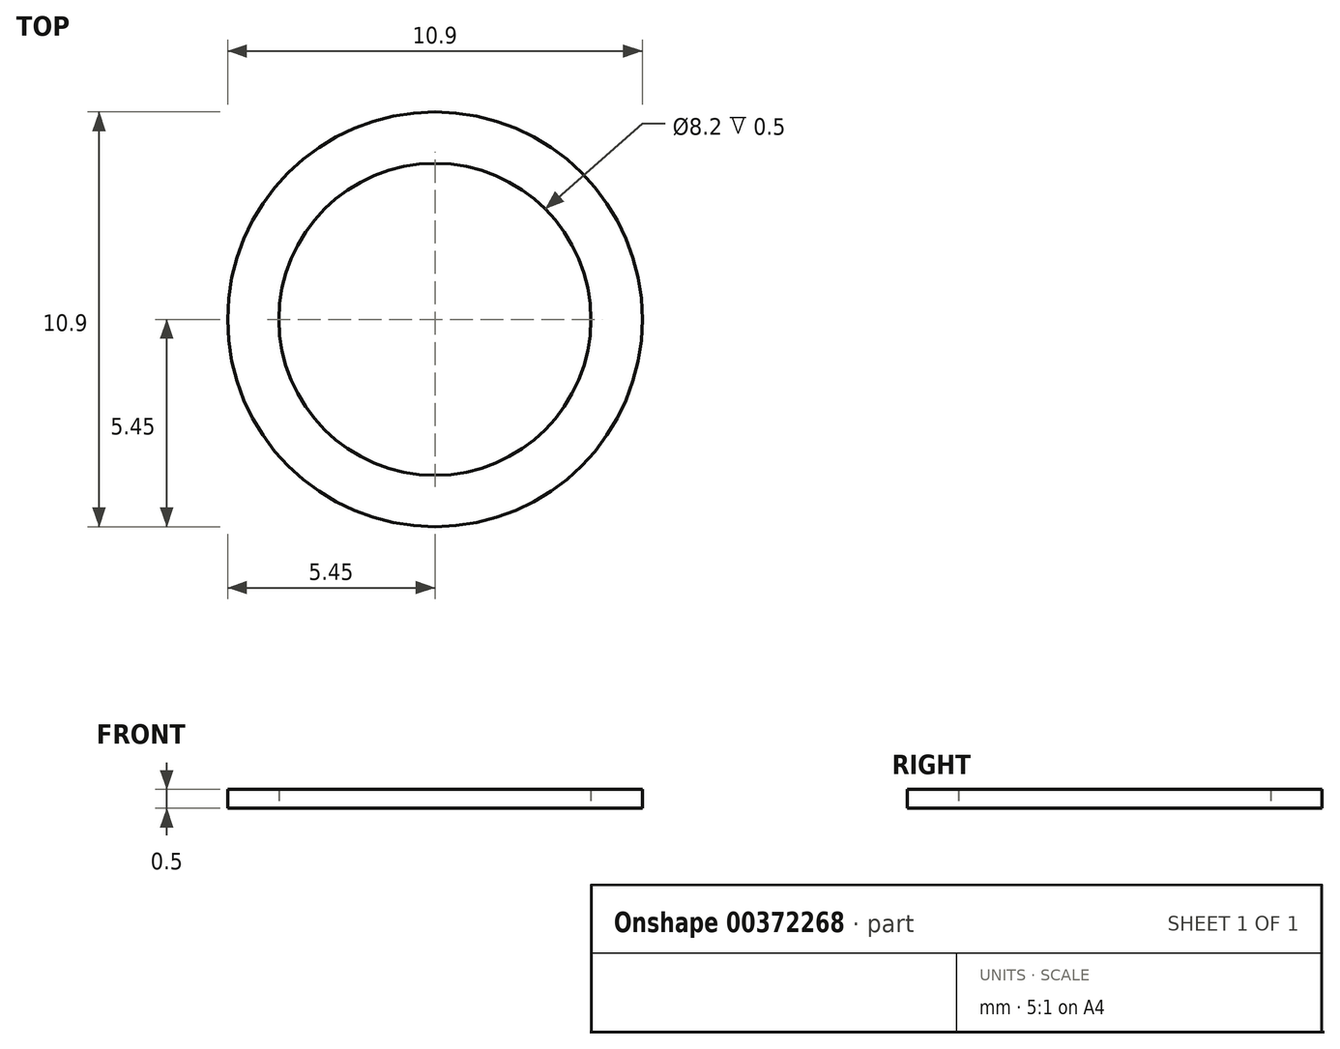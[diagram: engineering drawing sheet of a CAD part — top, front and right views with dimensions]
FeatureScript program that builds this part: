
annotation { "Feature Type Name" : "Feature", "Feature Type Description" : "" }
export const myFeature = defineFeature(function(context is Context, id is Id, definition is map)
    precondition{}
    {
        {
            var Q0;
            Q0=qCreatedBy(makeId("Top.planeOp"),FACE);
            var sketch = newSketch(context, id + "F0", { "sketchPlane" : qUnion([Q0])});
            skCircle(sketch, "E0", {"center": v(0, 0) * mm, "radius": 4.1 * mm});
            skCircle(sketch, "E1", {"center": v(0, 0) * mm, "radius": 5.45 * mm});
            skSolve(sketch);
        }
        {
            var Q0;
            Q0=makeQuery(id+"F0.imprint","IMPRINT",FACE,{"disambiguationData":[TD([[makeQuery(id+"F0.imprint","IMPRINT",EDGE,{"derivedFrom":sQuery(id+"F0.wireOp",EDGE,"E0")}),-1.0]])]});
            extrude(context, id + "F1", {"entities" : qUnion([Q0]), "depth" : 0.5 * mm});
        }
    });
